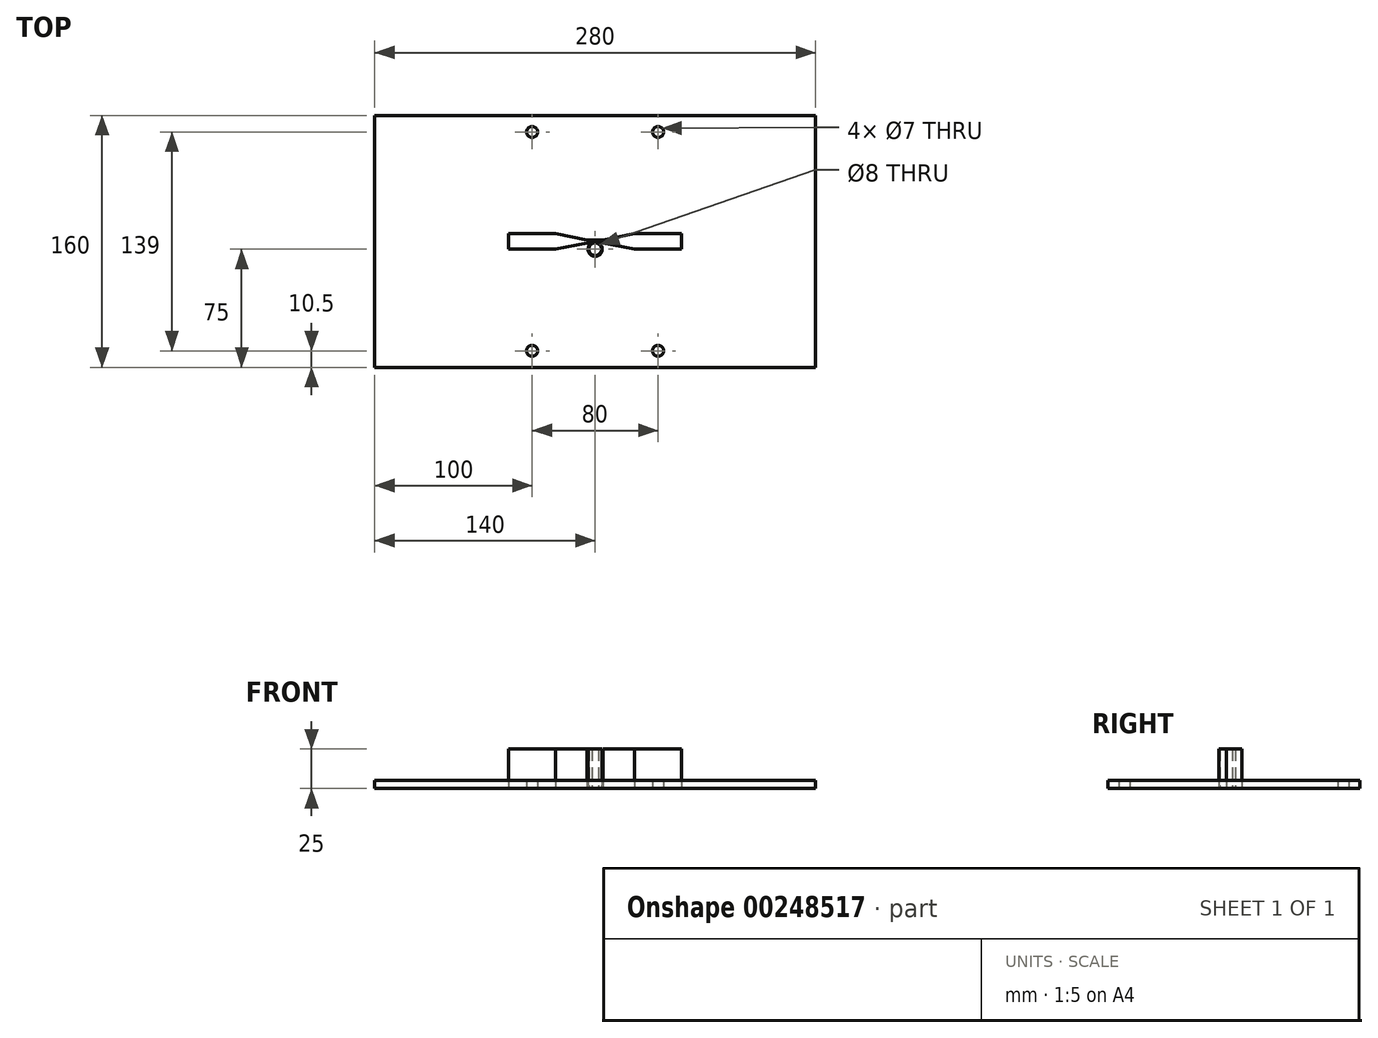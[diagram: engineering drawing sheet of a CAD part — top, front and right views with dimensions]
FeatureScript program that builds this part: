
annotation { "Feature Type Name" : "Feature", "Feature Type Description" : "" }
export const myFeature = defineFeature(function(context is Context, id is Id, definition is map)
    precondition{}
    {
        {
            var Q0;
            Q0=qCreatedBy(makeId("Top.planeOp"),FACE);
            var sketch = newSketch(context, id + "F0", { "sketchPlane" : qUnion([Q0])});
            skLineSegment(sketch, "E0", {"start": v(-140, 80) * mm, "end": v(140, 80) * mm});
            skLineSegment(sketch, "E1", {"start": v(140, 80) * mm, "end": v(140, -80) * mm});
            skLineSegment(sketch, "E2", {"start": v(140, -80) * mm, "end": v(-140, -80) * mm});
            skLineSegment(sketch, "E3", {"start": v(-140, -80) * mm, "end": v(-140, 80) * mm});
            skLineSegment(sketch, "E4", {"start": v(0, 80) * mm, "end": v(0, -80) * mm, "construction": true});
            skLineSegment(sketch, "E5", {"start": v(140, 0) * mm, "end": v(-140, 0) * mm, "construction": true});
            skCircle(sketch, "E6", {"center": v(-40, 69.5) * mm, "radius": 3.5 * mm});
            skCircle(sketch, "E7.MirrorC", {"center": v(-40, -69.5) * mm, "radius": 3.5 * mm});
            skCircle(sketch, "E8.MirrorC", {"center": v(40, -69.5) * mm, "radius": 3.5 * mm});
            skCircle(sketch, "E9.MirrorC", {"center": v(40, 69.5) * mm, "radius": 3.5 * mm});
            skSolve(sketch);
        }
        {
            var Q0;
            Q0=makeQuery(id+"F0.imprint","IMPRINT",FACE,{"disambiguationData":[TD([[makeQuery(id+"F0.imprint","IMPRINT",EDGE,{"derivedFrom":sQuery(id+"F0.wireOp",EDGE,"E0")}),-1.0]])]});
            extrude(context, id + "F1", {"entities" : qUnion([Q0]), "depth" : 5 * mm});
        }
        {
            var Q0;
            Q0=makeQuery(id+"F0.imprint","IMPRINT",FACE,{"disambiguationData":[TD([[makeQuery(id+"F0.imprint","IMPRINT",EDGE,{"derivedFrom":sQuery(id+"F0.wireOp",EDGE,"E0")}),-1.0]])]});
            var sketch = newSketch(context, id + "F2", { "sketchPlane" : qUnion([Q0])});
            skLineSegment(sketch, "E10.0", {"start": v(0, 80) * mm, "end": v(0, -80) * mm, "construction": true});
            skLineSegment(sketch, "E10.1", {"start": v(140, 0) * mm, "end": v(-140, 0) * mm, "construction": true});
            skLineSegment(sketch, "E11", {"start": v(0, 1) * mm, "end": v(-5, 1) * mm});
            skLineSegment(sketch, "E12", {"start": v(-5, 1) * mm, "end": v(-25, 5) * mm});
            skLineSegment(sketch, "E13", {"start": v(-25, 5) * mm, "end": v(-55, 5) * mm});
            skLineSegment(sketch, "E14", {"start": v(-55, 5) * mm, "end": v(-55, 0) * mm});
            skLineSegment(sketch, "E15", {"start": v(-55, 0) * mm, "end": v(-55, -5) * mm});
            skLineSegment(sketch, "E16", {"start": v(-55, -5) * mm, "end": v(-25, -5) * mm});
            skLineSegment(sketch, "E17", {"start": v(-25, -5) * mm, "end": v(-5, -1) * mm});
            skLineSegment(sketch, "E18", {"start": v(-5, -1) * mm, "end": v(0, -1) * mm});
            skLineSegment(sketch, "E19", {"start": v(0, -1) * mm, "end": v(5, -1) * mm});
            skLineSegment(sketch, "E20", {"start": v(5, -1) * mm, "end": v(25, -5) * mm});
            skLineSegment(sketch, "E21", {"start": v(25, -5) * mm, "end": v(55, -5) * mm});
            skLineSegment(sketch, "E22", {"start": v(55, -5) * mm, "end": v(55, 5) * mm});
            skLineSegment(sketch, "E23", {"start": v(55, 5) * mm, "end": v(25, 5) * mm});
            skLineSegment(sketch, "E24", {"start": v(25, 5) * mm, "end": v(5, 1) * mm});
            skLineSegment(sketch, "E25", {"start": v(5, 1) * mm, "end": v(0, 1) * mm});
            skLineSegment(sketch, "E26", {"start": v(0, 0) * mm, "end": v(0, -5) * mm});
            skCircle(sketch, "E27", {"center": v(0, -5) * mm, "radius": 4 * mm});
            skCircle(sketch, "E28", {"center": v(0, -5) * mm, "radius": 4.5 * mm});
            skSolve(sketch);
        }
        {
            var Q0;
            {var subQ0=sQuery(id+"F2.wireOp",EDGE,"E26");var subQ3=sQuery(id+"F2.wireOp",EDGE,"E28");var subQ5=makeQuery(id+"F2.imprint","INTERSECT",VERTEX,{"derivedFrom":[subQ0,subQ3]});Q0=makeQuery(id+"F2.imprint","IMPRINT",FACE,{"disambiguationData":[TD([[makeQuery(id+"F2.imprint","IMPRINT",EDGE,{"disambiguationData":[TD([[subQ5,-1.0]])],"derivedFrom":subQ3}),1.0]])]});}
            var Q1;
            {var subQ0=sQuery(id+"F2.wireOp",EDGE,"E26");var subQ3=sQuery(id+"F2.wireOp",EDGE,"E28");var subQ5=makeQuery(id+"F2.imprint","INTERSECT",VERTEX,{"derivedFrom":[subQ0,subQ3]});Q1=makeQuery(id+"F2.imprint","IMPRINT",FACE,{"disambiguationData":[TD([[makeQuery(id+"F2.imprint","IMPRINT",EDGE,{"disambiguationData":[TD([[subQ5,1.0]])],"derivedFrom":subQ3}),1.0]])]});}
            var Q2;
            {var subQ0=sQuery(id+"F2.wireOp",EDGE,"E27");Q2=makeQuery(id+"F2.imprint","IMPRINT",FACE,{"disambiguationData":[TD([[makeQuery(id+"F2.imprint","IMPRINT",EDGE,{"derivedFrom":subQ0}),-1.0]])]});}
            var Q3;
            Q3=makeQuery(id+"F2.imprint","IMPRINT",FACE,{"disambiguationData":[TD([[makeQuery(id+"F2.imprint","IMPRINT",EDGE,{"derivedFrom":sQuery(id+"F2.wireOp",EDGE,"E11")}),1.0]])]});
            extrude(context, id + "F3", {"entities" : qUnion([Q0, Q1, Q2, Q3]), "depth" : 25 * mm});
        }
    });
